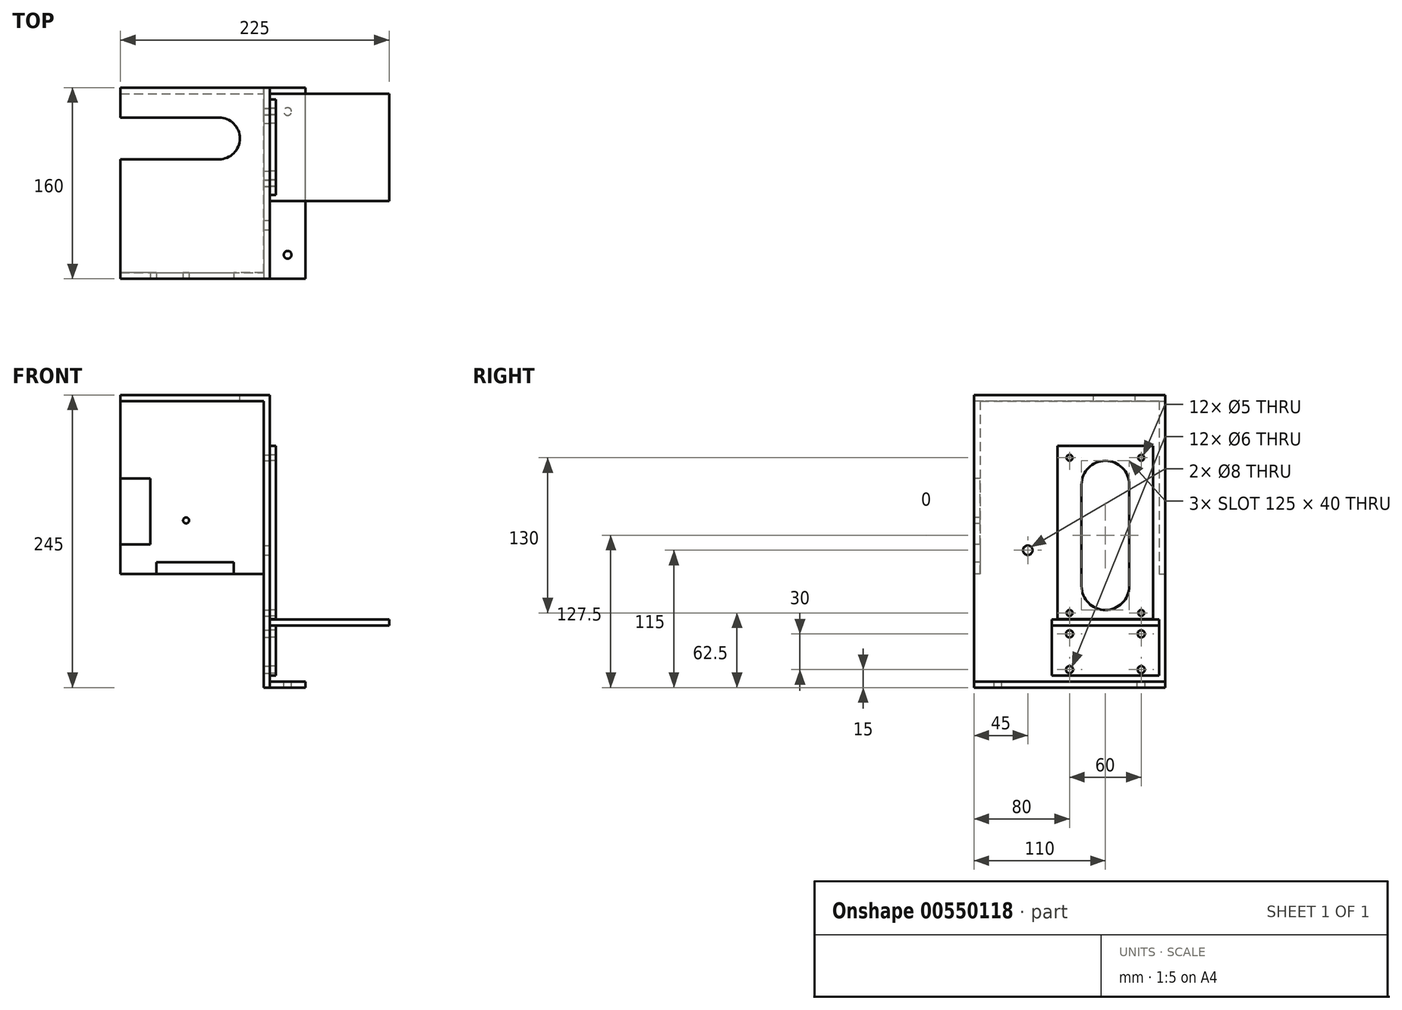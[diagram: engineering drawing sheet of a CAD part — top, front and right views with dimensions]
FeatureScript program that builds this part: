
annotation { "Feature Type Name" : "Feature", "Feature Type Description" : "" }
export const myFeature = defineFeature(function(context is Context, id is Id, definition is map)
    precondition{}
    {
        {
            var Q0;
            Q0=qCreatedBy(makeId("Front.planeOp"),FACE);
            var sketch = newSketch(context, id + "F0", { "sketchPlane" : qUnion([Q0])});
            skLineSegment(sketch, "E0.bottom", {"start": v(-62.5, 122.5) * mm, "end": v(62.5, 122.5) * mm});
            skLineSegment(sketch, "E0.right", {"start": v(62.5, 122.5) * mm, "end": v(62.5, -122.5) * mm});
            skPoint(sketch, "E0.middle", {"position": v(0, 0) * mm});
            skLineSegment(sketch, "E1.0", {"start": v(-62.5, 117.5) * mm, "end": v(57.5, 117.5) * mm});
            skLineSegment(sketch, "E2.0", {"start": v(57.5, 117.5) * mm, "end": v(57.5, -122.5) * mm});
            skLineSegment(sketch, "E3.trimOffspring", {"start": v(62.5, 117.5) * mm, "end": v(62.5, 117.5) * mm});
            skLineSegment(sketch, "E4", {"start": v(-62.5, 122.5) * mm, "end": v(-62.5, 117.5) * mm});
            skLineSegment(sketch, "E5", {"start": v(62.5, -122.5) * mm, "end": v(57.5, -122.5) * mm});
            skSolve(sketch);
        }
        {
            var Q0;
            Q0=makeQuery(id+"F0.imprint","IMPRINT",FACE,{"disambiguationData":[TD([[makeQuery(id+"F0.imprint","IMPRINT",EDGE,{"derivedFrom":sQuery(id+"F0.wireOp",EDGE,"E1.0")}),1.0]])]});
            var Q1;
            {var subQ3=sQuery(id+"F0.wireOp",EDGE,"E3.trimOffspring");Q1=makeQuery(id+"F0.imprint","IMPRINT",FACE,{"disambiguationData":[TD([[makeQuery(id+"F0.imprint","IMPRINT",EDGE,{"derivedFrom":subQ3}),-1.0]])]});}
            var Q2;
            {var subQ5=sQuery(id+"F0.wireOp",EDGE,"E3.trimOffspring");Q2=makeQuery(id+"F0.imprint","IMPRINT",FACE,{"disambiguationData":[TD([[makeQuery(id+"F0.imprint","IMPRINT",EDGE,{"derivedFrom":subQ5}),1.0]])]});}
            extrude(context, id + "F1", {"entities" : qUnion([Q0, Q1, Q2]), "depth" : 160 * mm, "offsetDistance" : 25 * mm});
        }
        {
            var Q0;
            Q0=makeQuery(id+"F1.opExtrude","CAP_FACE",FACE,{"disambiguationData":[OSD([sQuery(id+"F0.wireOp",EDGE,"E0.bottom"),sQuery(id+"F0.wireOp",EDGE,"E0.right"),sQuery(id+"F0.wireOp",EDGE,"E1.0"),sQuery(id+"F0.wireOp",EDGE,"E2.0"),sQuery(id+"F0.wireOp",EDGE,"E4"),sQuery(id+"F0.wireOp",EDGE,"E5")])],"isStart":false});
            var sketch = newSketch(context, id + "F2", { "sketchPlane" : qUnion([Q0])});
            skLineSegment(sketch, "E6.top", {"start": v(62.5, -27.5) * mm, "end": v(-62.5, -27.5) * mm});
            skLineSegment(sketch, "E6.left", {"start": v(62.5, 122.5) * mm, "end": v(62.5, -27.5) * mm});
            skLineSegment(sketch, "E6.right", {"start": v(-62.5, 122.5) * mm, "end": v(-62.5, -27.5) * mm});
            skLineSegment(sketch, "E7", {"start": v(62.5, 122.5) * mm, "end": v(-62.5, 122.5) * mm});
            skSolve(sketch);
        }
        {
            var Q0;
            Q0=qSketchRegion(id+"F2",true);
            extrude(context, id + "F3", {"entities" : qUnion([Q0]), "operationType" : NewBodyOperationType.ADD, "oppositeDirection" : true, "depth" : 5 * mm, "offsetDistance" : 25 * mm});
        }
        {
            var Q0;
            Q0=makeQuery(id+"F3.boolean.opBoolean","MERGE",FACE,{"derivedFrom":[makeQuery(id+"F1.opExtrude","CAP_FACE",FACE,{"disambiguationData":[OSD([sQuery(id+"F0.wireOp",EDGE,"E0.bottom"),sQuery(id+"F0.wireOp",EDGE,"E0.right"),sQuery(id+"F0.wireOp",EDGE,"E1.0"),sQuery(id+"F0.wireOp",EDGE,"E2.0"),sQuery(id+"F0.wireOp",EDGE,"E4"),sQuery(id+"F0.wireOp",EDGE,"E5")])],"isStart":false}),makeQuery(id+"F3.opExtrude","CAP_FACE",FACE,{"disambiguationData":[OSD([sQuery(id+"F2.wireOp",EDGE,"E6.top"),sQuery(id+"F2.wireOp",EDGE,"E6.left"),sQuery(id+"F2.wireOp",EDGE,"E6.right"),sQuery(id+"F2.wireOp",EDGE,"E7")])],"isStart":true})]});
            cPlane(context, id + "F4", {"entities" : qUnion([Q0]), "cplaneType" : CPlaneType.OFFSET, "offset" : 80 * mm, "oppositeDirection" : true, "width" : 150 * mm, "height" : 150 * mm});
        }
        {
            var Q0;
            Q0=makeQuery(id+"F1.opExtrude","SWEPT_BODY",BODY,{"disambiguationData":[OSD([sQuery(id+"F0.wireOp",EDGE,"E0.bottom"),sQuery(id+"F0.wireOp",EDGE,"E0.right"),sQuery(id+"F0.wireOp",EDGE,"E1.0"),sQuery(id+"F0.wireOp",EDGE,"E2.0"),sQuery(id+"F0.wireOp",EDGE,"E4"),sQuery(id+"F0.wireOp",EDGE,"E5")])]});
            var Q1;
            Q1=qCreatedBy(id+"F4.planeOp",FACE);
            mirror(context, id + "F5", {"entities" : qUnion([Q0]), "mirrorPlane" : qUnion([Q1])});
        }
        {
            var Q0;
            Q0=makeQuery(id+"F1.opExtrude","SWEPT_FACE",FACE,{"disambiguationData":[OSD([sQuery(id+"F0.wireOp",EDGE,"E0.bottom")])]});
            var sketch = newSketch(context, id + "F6", { "sketchPlane" : qUnion([Q0])});
            skLineSegment(sketch, "E8.0", {"start": v(-62.5, -60) * mm, "end": v(20, -60) * mm});
            skLineSegment(sketch, "E9.0", {"start": v(-62.5, -25) * mm, "end": v(20, -25) * mm});
            skLineSegment(sketch, "E10", {"start": v(-62.5, -25) * mm, "end": v(-62.5, -60) * mm});
            skArc(sketch, "E11", {"start": v(20, -60) * mm, "mid": v(37.5, -42.5) * mm, "end": v(20, -25) * mm});
            skSolve(sketch);
        }
        {
            var Q0;
            Q0=qSketchRegion(id+"F6",true);
            extrude(context, id + "F7", {"entities" : qUnion([Q0]), "operationType" : NewBodyOperationType.REMOVE, "oppositeDirection" : true, "depth" : 25 * mm, "offsetDistance" : 25 * mm});
        }
        {
            var Q0;
            Q0=makeQuery(id+"F1.opExtrude","SWEPT_FACE",FACE,{"disambiguationData":[OSD([sQuery(id+"F0.wireOp",EDGE,"E0.right")])]});
            var sketch = newSketch(context, id + "F8", { "sketchPlane" : qUnion([Q0])});
            skLineSegment(sketch, "E12.bottom", {"start": v(-160, -122.5) * mm, "end": v(0, -122.5) * mm});
            skLineSegment(sketch, "E12.top", {"start": v(-160, -117.5) * mm, "end": v(0, -117.5) * mm});
            skLineSegment(sketch, "E12.left", {"start": v(-160, -122.5) * mm, "end": v(-160, -117.5) * mm});
            skLineSegment(sketch, "E12.right", {"start": v(0, -122.5) * mm, "end": v(0, -117.5) * mm});
            skSolve(sketch);
        }
        {
            var Q0;
            Q0=makeQuery(id+"F8.imprint","IMPRINT",FACE,{"disambiguationData":[TD([[makeQuery(id+"F8.imprint","IMPRINT",EDGE,{"derivedFrom":sQuery(id+"F8.wireOp",EDGE,"E12.bottom")}),1.0]])]});
            extrude(context, id + "F9", {"entities" : qUnion([Q0]), "depth" : 30 * mm, "offsetDistance" : 25 * mm});
        }
        {
            var Q0;
            Q0=makeQuery(id+"F9.opExtrude","SWEPT_FACE",FACE,{"disambiguationData":[OSD([sQuery(id+"F8.wireOp",EDGE,"E12.top")])]});
            var sketch = newSketch(context, id + "F10", { "sketchPlane" : qUnion([Q0])});
            skCircle(sketch, "E13", {"center": v(77.5, -140) * mm, "radius": 3.25 * mm});
            skCircle(sketch, "E14", {"center": v(77.5, -20) * mm, "radius": 3.25 * mm});
            skSolve(sketch);
        }
        {
            var Q0;
            Q0=qSketchRegion(id+"F10",true);
            extrude(context, id + "F11", {"entities" : qUnion([Q0]), "operationType" : NewBodyOperationType.REMOVE, "oppositeDirection" : true, "depth" : 25 * mm, "offsetDistance" : 25 * mm});
        }
        {
            var Q0;
            Q0=makeQuery(id+"F1.opExtrude","SWEPT_FACE",FACE,{"disambiguationData":[OSD([sQuery(id+"F0.wireOp",EDGE,"E0.right")])]});
            var sketch = newSketch(context, id + "F12", { "sketchPlane" : qUnion([Q0])});
            skLineSegment(sketch, "E15.0", {"start": v(-30, 47.5) * mm, "end": v(-30, -37.5) * mm});
            skLineSegment(sketch, "E16.0", {"start": v(-70, 47.5) * mm, "end": v(-70, -37.5) * mm});
            skArc(sketch, "E17", {"start": v(-30, 47.5) * mm, "mid": v(-50, 67.5) * mm, "end": v(-70, 47.5) * mm});
            skArc(sketch, "E18", {"start": v(-70, -37.5) * mm, "mid": v(-50, -57.5) * mm, "end": v(-30, -37.5) * mm});
            skSolve(sketch);
        }
        {
            var Q0;
            Q0=makeQuery(id+"F12.imprint","IMPRINT",FACE,{"disambiguationData":[TD([[makeQuery(id+"F12.imprint","IMPRINT",EDGE,{"derivedFrom":sQuery(id+"F12.wireOp",EDGE,"E15.0")}),-1.0]])]});
            extrude(context, id + "F13", {"entities" : qUnion([Q0]), "operationType" : NewBodyOperationType.REMOVE, "endBound" : BoundingType.UP_TO_NEXT, "oppositeDirection" : true, "depth" : 25 * mm, "offsetDistance" : 25 * mm});
        }
        {
            var Q0;
            Q0=makeQuery(id+"F1.opExtrude","SWEPT_FACE",FACE,{"disambiguationData":[OSD([sQuery(id+"F0.wireOp",EDGE,"E0.right")])]});
            var sketch = newSketch(context, id + "F14", { "sketchPlane" : qUnion([Q0])});
            skCircle(sketch, "E19", {"center": v(-80, 70) * mm, "radius": 2.5 * mm});
            skCircle(sketch, "E20", {"center": v(-20, 70) * mm, "radius": 2.5 * mm});
            skCircle(sketch, "E21.MirrorC", {"center": v(-20, -60) * mm, "radius": 2.5 * mm});
            skCircle(sketch, "E22.MirrorC", {"center": v(-80, -60) * mm, "radius": 2.5 * mm});
            skPoint(sketch, "E23.orphan", {"position": v(-50, -57.5) * mm});
            skPoint(sketch, "E24.trimOffspring.end.orphan", {"position": v(-160, 5) * mm});
            skSolve(sketch);
        }
        {
            var Q0;
            Q0=qSketchRegion(id+"F14",true);
            extrude(context, id + "F15", {"entities" : qUnion([Q0]), "operationType" : NewBodyOperationType.REMOVE, "endBound" : BoundingType.UP_TO_NEXT, "oppositeDirection" : true, "depth" : 25 * mm, "offsetDistance" : 25 * mm});
        }
        {
            var Q0;
            Q0=makeQuery(id+"F3.boolean.opBoolean","MERGE",FACE,{"derivedFrom":[makeQuery(id+"F1.opExtrude","CAP_FACE",FACE,{"disambiguationData":[OSD([sQuery(id+"F0.wireOp",EDGE,"E0.bottom"),sQuery(id+"F0.wireOp",EDGE,"E0.right"),sQuery(id+"F0.wireOp",EDGE,"E1.0"),sQuery(id+"F0.wireOp",EDGE,"E2.0"),sQuery(id+"F0.wireOp",EDGE,"E4"),sQuery(id+"F0.wireOp",EDGE,"E5")])],"isStart":false}),makeQuery(id+"F3.opExtrude","CAP_FACE",FACE,{"disambiguationData":[OSD([sQuery(id+"F2.wireOp",EDGE,"E6.top"),sQuery(id+"F2.wireOp",EDGE,"E6.left"),sQuery(id+"F2.wireOp",EDGE,"E6.right"),sQuery(id+"F2.wireOp",EDGE,"E7")])],"isStart":true})]});
            var sketch = newSketch(context, id + "F16", { "sketchPlane" : qUnion([Q0])});
            skLineSegment(sketch, "E25.0", {"start": v(-62.5, 52.5) * mm, "end": v(-37.5, 52.5) * mm});
            skLineSegment(sketch, "E26.0", {"start": v(-62.5, -2.5) * mm, "end": v(-37.5, -2.5) * mm});
            skLineSegment(sketch, "E27.0", {"start": v(-37.5, 52.5) * mm, "end": v(-37.5, -2.5) * mm});
            skLineSegment(sketch, "E28", {"start": v(-62.5, 52.5) * mm, "end": v(-62.5, -2.5) * mm});
            skSolve(sketch);
        }
        {
            var Q0;
            Q0=qSketchRegion(id+"F16",true);
            extrude(context, id + "F17", {"entities" : qUnion([Q0]), "operationType" : NewBodyOperationType.REMOVE, "endBound" : BoundingType.UP_TO_NEXT, "oppositeDirection" : true, "depth" : 25 * mm, "offsetDistance" : 25 * mm});
        }
        {
            var Q0;
            Q0=makeQuery(id+"F3.boolean.opBoolean","MERGE",FACE,{"derivedFrom":[makeQuery(id+"F1.opExtrude","CAP_FACE",FACE,{"disambiguationData":[OSD([sQuery(id+"F0.wireOp",EDGE,"E0.bottom"),sQuery(id+"F0.wireOp",EDGE,"E0.right"),sQuery(id+"F0.wireOp",EDGE,"E1.0"),sQuery(id+"F0.wireOp",EDGE,"E2.0"),sQuery(id+"F0.wireOp",EDGE,"E4"),sQuery(id+"F0.wireOp",EDGE,"E5")])],"isStart":false}),makeQuery(id+"F3.opExtrude","CAP_FACE",FACE,{"disambiguationData":[OSD([sQuery(id+"F2.wireOp",EDGE,"E6.top"),sQuery(id+"F2.wireOp",EDGE,"E6.left"),sQuery(id+"F2.wireOp",EDGE,"E6.right"),sQuery(id+"F2.wireOp",EDGE,"E7")])],"isStart":true})]});
            var sketch = newSketch(context, id + "F18", { "sketchPlane" : qUnion([Q0])});
            skCircle(sketch, "E29", {"center": v(-7.5, 17.5) * mm, "radius": 2.5 * mm});
            skPoint(sketch, "E30.orphan", {"position": v(-7.5, 117.5) * mm});
            skLineSegment(sketch, "E31.0", {"start": v(-32.5, -17.5) * mm, "end": v(-32.5, -27.5) * mm});
            skLineSegment(sketch, "E32.0", {"start": v(32.5, -17.5) * mm, "end": v(-32.5, -17.5) * mm});
            skLineSegment(sketch, "E33", {"start": v(32.5, -17.5) * mm, "end": v(32.5, -27.5) * mm});
            skLineSegment(sketch, "E34", {"start": v(32.5, -27.5) * mm, "end": v(-32.5, -27.5) * mm});
            skSolve(sketch);
        }
        {
            var Q0;
            Q0=qSketchRegion(id+"F18",true);
            extrude(context, id + "F19", {"entities" : qUnion([Q0]), "operationType" : NewBodyOperationType.REMOVE, "endBound" : BoundingType.UP_TO_NEXT, "oppositeDirection" : true, "depth" : 25 * mm, "offsetDistance" : 25 * mm});
        }
        {
            var Q0;
            Q0=makeQuery(id+"F1.opExtrude","SWEPT_FACE",FACE,{"disambiguationData":[OSD([sQuery(id+"F0.wireOp",EDGE,"E0.right")])]});
            var sketch = newSketch(context, id + "F20", { "sketchPlane" : qUnion([Q0])});
            skCircle(sketch, "E35", {"center": v(-115, -7.5) * mm, "radius": 4 * mm});
            skCircle(sketch, "E36", {"center": v(-80, -77.5) * mm, "radius": 3 * mm});
            skCircle(sketch, "E37", {"center": v(-20, -77.5) * mm, "radius": 3 * mm});
            skCircle(sketch, "E38", {"center": v(-80, -107.5) * mm, "radius": 3 * mm});
            skCircle(sketch, "E39", {"center": v(-20, -107.5) * mm, "radius": 3 * mm});
            skSolve(sketch);
        }
        {
            var Q0;
            Q0=qSketchRegion(id+"F20",true);
            extrude(context, id + "F21", {"entities" : qUnion([Q0]), "operationType" : NewBodyOperationType.REMOVE, "endBound" : BoundingType.UP_TO_NEXT, "oppositeDirection" : true, "depth" : 25 * mm, "offsetDistance" : 25 * mm});
        }
        {
            var Q0;
            Q0=makeQuery(id+"F1.opExtrude","SWEPT_FACE",FACE,{"disambiguationData":[OSD([sQuery(id+"F0.wireOp",EDGE,"E0.right")])]});
            var sketch = newSketch(context, id + "F22", { "sketchPlane" : qUnion([Q0])});
            skLineSegment(sketch, "E40.bottom", {"start": v(-10, 80) * mm, "end": v(-90, 80) * mm});
            skLineSegment(sketch, "E40.top", {"start": v(-10, -70) * mm, "end": v(-90, -70) * mm});
            skLineSegment(sketch, "E40.left", {"start": v(-10, 80) * mm, "end": v(-10, -70) * mm});
            skLineSegment(sketch, "E40.right", {"start": v(-90, 80) * mm, "end": v(-90, -70) * mm});
            skPoint(sketch, "E40.middle", {"position": v(-50, 5) * mm});
            skPoint(sketch, "E40.middle.positionSnap0", {"position": v(-50, 67.5) * mm});
            skPoint(sketch, "E40.middle.positionSnap1", {"position": v(-30, 5) * mm});
            skPoint(sketch, "E40.centerSnap0", {"position": v(-50, 67.5) * mm});
            skPoint(sketch, "E40.centerSnap1", {"position": v(-30, 5) * mm});
            skCircle(sketch, "E41.0", {"center": v(-80, 70) * mm, "radius": 2.5 * mm});
            skCircle(sketch, "E42.0", {"center": v(-20, 70) * mm, "radius": 2.5 * mm});
            skCircle(sketch, "E43.0", {"center": v(-80, -60) * mm, "radius": 2.5 * mm});
            skCircle(sketch, "E44.0", {"center": v(-20, -60) * mm, "radius": 2.5 * mm});
            skSolve(sketch);
        }
        {
            var Q0;
            Q0=makeQuery(id+"F22.imprint","IMPRINT",FACE,{"disambiguationData":[TD([[makeQuery(id+"F22.imprint","IMPRINT",EDGE,{"derivedFrom":sQuery(id+"F22.wireOp",EDGE,"E40.bottom")}),1.0]])]});
            extrude(context, id + "F23", {"entities" : qUnion([Q0]), "depth" : 5 * mm, "offsetDistance" : 25 * mm});
        }
        {
            var Q0;
            Q0=makeQuery(id+"F1.opExtrude","SWEPT_FACE",FACE,{"disambiguationData":[OSD([sQuery(id+"F0.wireOp",EDGE,"E0.right")])]});
            var sketch = newSketch(context, id + "F24", { "sketchPlane" : qUnion([Q0])});
            skLineSegment(sketch, "E45.bottom", {"start": v(-5, -112.5) * mm, "end": v(-95, -112.5) * mm});
            skLineSegment(sketch, "E45.top", {"start": v(-5, -70.5) * mm, "end": v(-95, -70.5) * mm});
            skLineSegment(sketch, "E45.left", {"start": v(-5, -112.5) * mm, "end": v(-5, -70.5) * mm});
            skLineSegment(sketch, "E45.right", {"start": v(-95, -112.5) * mm, "end": v(-95, -70.5) * mm});
            skPoint(sketch, "E45.middle", {"position": v(-50, -91.5) * mm});
            skPoint(sketch, "E45.middle.positionSnap0", {"position": v(-50, -57.5) * mm});
            skPoint(sketch, "E45.centerSnap0", {"position": v(-50, -57.5) * mm});
            skPoint(sketch, "E46", {"position": v(-20, -107.5) * mm});
            skCircle(sketch, "E47.0", {"center": v(-80, -77.5) * mm, "radius": 3 * mm});
            skCircle(sketch, "E48.0", {"center": v(-80, -107.5) * mm, "radius": 3 * mm});
            skCircle(sketch, "E49.0", {"center": v(-20, -77.5) * mm, "radius": 3 * mm});
            skCircle(sketch, "E50.0", {"center": v(-20, -107.5) * mm, "radius": 3 * mm});
            skSolve(sketch);
        }
        {
            var Q0;
            Q0=makeQuery(id+"F23.opExtrude","CAP_FACE",FACE,{"disambiguationData":[OSD([sQuery(id+"F12.wireOp",EDGE,"E15.0"),sQuery(id+"F12.wireOp",EDGE,"E16.0"),sQuery(id+"F12.wireOp",EDGE,"E17"),sQuery(id+"F12.wireOp",EDGE,"E18"),sQuery(id+"F22.wireOp",EDGE,"E40.bottom"),sQuery(id+"F22.wireOp",EDGE,"E40.top"),sQuery(id+"F22.wireOp",EDGE,"E40.left"),sQuery(id+"F22.wireOp",EDGE,"E40.right"),sQuery(id+"F22.wireOp",EDGE,"E41.0"),sQuery(id+"F22.wireOp",EDGE,"E42.0"),sQuery(id+"F22.wireOp",EDGE,"E43.0"),sQuery(id+"F22.wireOp",EDGE,"E44.0")])],"isStart":false});
            var sketch = newSketch(context, id + "F25", { "sketchPlane" : qUnion([Q0])});
            skLineSegment(sketch, "E51.bottom", {"start": v(-90, -70) * mm, "end": v(-10, -70) * mm});
            skLineSegment(sketch, "E51.top", {"start": v(-90, -65) * mm, "end": v(-10, -65) * mm});
            skLineSegment(sketch, "E51.left", {"start": v(-90, -70) * mm, "end": v(-90, -65) * mm});
            skLineSegment(sketch, "E51.right", {"start": v(-10, -70) * mm, "end": v(-10, -65) * mm});
            skSolve(sketch);
        }
        {
            var Q0;
            Q0 = qSketchRegion(id + "F25", true);
            var Q1;
            Q1=makeQuery(id+"F1.opExtrude","SWEPT_FACE",FACE,{"disambiguationData":[OSD([sQuery(id+"F0.wireOp",EDGE,"E0.right")])]});
            extrude(context, id + "F26", {"entities" : qUnion([Q0]), "operationType" : NewBodyOperationType.REMOVE, "endBound" : BoundingType.UP_TO_SURFACE, "oppositeDirection" : true, "depth" : 25 * mm, "endBoundEntityFace" : qUnion([Q1]), "offsetDistance" : 25 * mm});
        }
        {
            var Q0;
            Q0 = qSketchRegion(id + "F24", true);
            extrude(context, id + "F27", {"entities" : qUnion([Q0]), "depth" : 5 * mm, "offsetDistance" : 25 * mm});
        }
        {
            var Q0;
            Q0=makeQuery(id+"F1.opExtrude","SWEPT_FACE",FACE,{"disambiguationData":[OSD([sQuery(id+"F0.wireOp",EDGE,"E0.right")])]});
            var sketch = newSketch(context, id + "F28", { "sketchPlane" : qUnion([Q0])});
            skLineSegment(sketch, "E52.bottom", {"start": v(-5, -65.5) * mm, "end": v(-95, -65.5) * mm});
            skLineSegment(sketch, "E52.top", {"start": v(-5, -70.5) * mm, "end": v(-95, -70.5) * mm});
            skLineSegment(sketch, "E52.left", {"start": v(-5, -65.5) * mm, "end": v(-5, -70.5) * mm});
            skLineSegment(sketch, "E52.right", {"start": v(-95, -65.5) * mm, "end": v(-95, -70.5) * mm});
            skPoint(sketch, "E52.middle", {"position": v(-50, -68) * mm});
            skPoint(sketch, "E52.middle.positionSnap0", {"position": v(-50, -57.5) * mm});
            skPoint(sketch, "E52.centerSnap0", {"position": v(-50, -57.5) * mm});
            skSolve(sketch);
        }
        {
            var Q0;
            Q0 = qSketchRegion(id + "F28", true);
            extrude(context, id + "F29", {"entities" : qUnion([Q0]), "depth" : 100 * mm, "offsetDistance" : 25 * mm});
        }
    });
